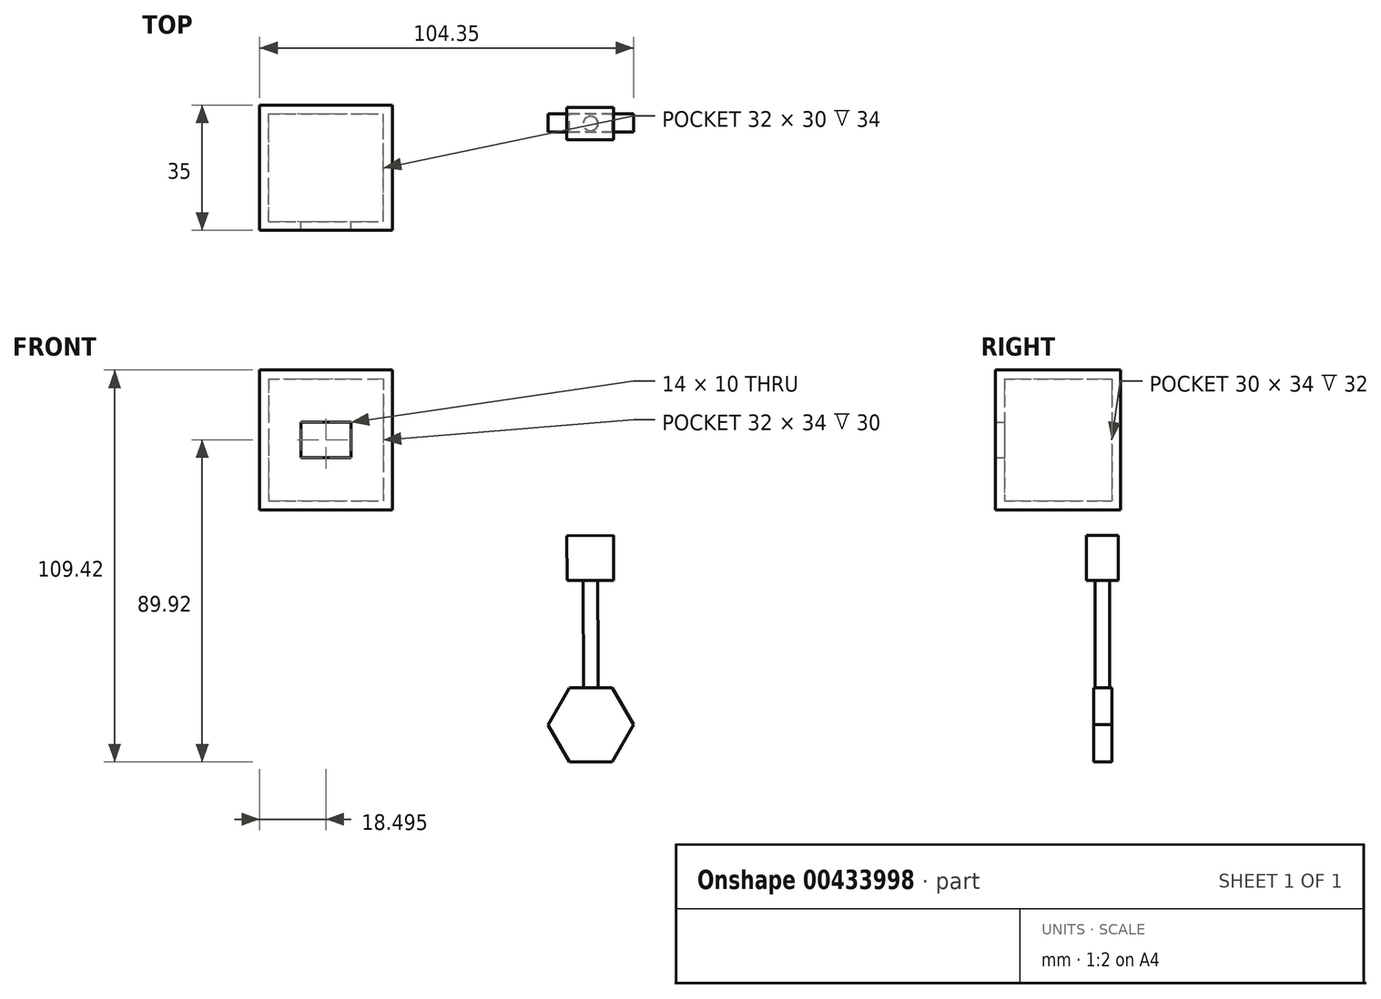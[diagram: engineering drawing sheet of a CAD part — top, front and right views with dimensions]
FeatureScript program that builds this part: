
annotation { "Feature Type Name" : "Feature", "Feature Type Description" : "" }
export const myFeature = defineFeature(function(context is Context, id is Id, definition is map)
    precondition{}
    {
        {
            var Q0;
            Q0=qCreatedBy(makeId("Front.planeOp"),FACE);
            var sketch = newSketch(context, id + "F0", { "sketchPlane" : qUnion([Q0])});
            skLineSegment(sketch, "E0.bottom", {"start": v(-54.76, 59.69) * mm, "end": v(-22.76, 59.69) * mm});
            skLineSegment(sketch, "E0.top", {"start": v(-54.76, 25.69) * mm, "end": v(-22.76, 25.69) * mm});
            skLineSegment(sketch, "E0.left", {"start": v(-54.76, 59.69) * mm, "end": v(-54.76, 25.69) * mm});
            skLineSegment(sketch, "E0.right", {"start": v(-22.76, 59.69) * mm, "end": v(-22.76, 25.69) * mm});
            skLineSegment(sketch, "E1.bottom", {"start": v(-45.76, 47.69) * mm, "end": v(-31.76, 47.69) * mm});
            skLineSegment(sketch, "E1.top", {"start": v(-45.76, 37.69) * mm, "end": v(-31.76, 37.69) * mm});
            skLineSegment(sketch, "E1.left", {"start": v(-45.76, 47.69) * mm, "end": v(-45.76, 37.69) * mm});
            skLineSegment(sketch, "E1.right", {"start": v(-31.76, 47.69) * mm, "end": v(-31.76, 37.69) * mm});
            skSolve(sketch);
        }
        {
            var Q0;
            Q0=makeQuery(id+"F0.imprint","IMPRINT",FACE,{"disambiguationData":[TD([[makeQuery(id+"F0.imprint","IMPRINT",EDGE,{"derivedFrom":sQuery(id+"F0.wireOp",EDGE,"E1.bottom")}),-1.0]])]});
            extrude(context, id + "F1", {"entities" : qUnion([Q0]), "depth" : 20 * mm});
        }
        {
            var Q0;
            Q0 = qSketchRegion(id + "F0", true);
            extrude(context, id + "F2", {"entities" : qUnion([Q0]), "operationType" : NewBodyOperationType.ADD, "depth" : 30 * mm});
        }
        {
            var Q0;
            Q0=makeQuery(id+"F2.opExtrude","SWEPT_FACE",FACE,{"disambiguationData":[OSD([sQuery(id+"F0.wireOp",EDGE,"E1.bottom")])]});
            var Q1;
            Q1=makeQuery(id+"F2.opExtrude","SWEPT_FACE",FACE,{"disambiguationData":[OSD([sQuery(id+"F0.wireOp",EDGE,"E1.right")])]});
            var Q2;
            Q2=makeQuery(id+"F2.opExtrude","SWEPT_FACE",FACE,{"disambiguationData":[OSD([sQuery(id+"F0.wireOp",EDGE,"E1.top")])]});
            var Q3;
            Q3=makeQuery(id+"F2.opExtrude","SWEPT_FACE",FACE,{"disambiguationData":[OSD([sQuery(id+"F0.wireOp",EDGE,"E1.left")])]});
            var Q4;
            Q4=makeQuery(id+"F1.opExtrude","CAP_FACE",FACE,{"disambiguationData":[OSD([sQuery(id+"F0.wireOp",EDGE,"E1.bottom"),sQuery(id+"F0.wireOp",EDGE,"E1.top"),sQuery(id+"F0.wireOp",EDGE,"E1.left"),sQuery(id+"F0.wireOp",EDGE,"E1.right")])],"isStart":false});
            shell(context, id + "F3", {"entities" : qUnion([Q0, Q1, Q2, Q3, Q4]), "thickness" : 2.5 * mm, "oppositeDirection" : true});
        }
        {
            var Q0;
            Q0=qCreatedBy(makeId("Front.planeOp"),FACE);
            var sketch = newSketch(context, id + "F4", { "sketchPlane" : qUnion([Q0])});
            skCircle(sketch, "E2.cCircle", {"center": v(35.15, -36.86) * mm, "radius": 10.34 * mm, "construction": true});
            skLineSegment(sketch, "E2.0", {"start": v(47.1, -36.81) * mm, "end": v(41.17, -47.17) * mm});
            skLineSegment(sketch, "E2.1", {"start": v(41.17, -47.17) * mm, "end": v(29.23, -47.23) * mm});
            skLineSegment(sketch, "E2.2", {"start": v(29.23, -47.23) * mm, "end": v(23.22, -36.92) * mm});
            skLineSegment(sketch, "E2.3", {"start": v(23.22, -36.92) * mm, "end": v(29.14, -26.55) * mm});
            skLineSegment(sketch, "E2.4", {"start": v(29.14, -26.55) * mm, "end": v(41.08, -26.5) * mm});
            skLineSegment(sketch, "E2.5", {"start": v(41.08, -26.5) * mm, "end": v(47.1, -36.81) * mm});
            skPoint(sketch, "E2.0.midPoint", {"position": v(44.13, -42) * mm});
            skSolve(sketch);
        }
        {
            var Q0;
            Q0=makeQuery(id+"F4.imprint","IMPRINT",FACE,{"disambiguationData":[TD([[makeQuery(id+"F4.imprint","IMPRINT",EDGE,{"derivedFrom":sQuery(id+"F4.wireOp",EDGE,"E2.0")}),-1.0]])]});
            extrude(context, id + "F5", {"entities" : qUnion([Q0]), "depth" : 5 * mm});
        }
        {
            var Q0;
            Q0=makeQuery(id+"F5.opExtrude","SWEPT_FACE",FACE,{"disambiguationData":[OSD([sQuery(id+"F4.wireOp",EDGE,"E2.4")])]});
            var sketch = newSketch(context, id + "F6", { "sketchPlane" : qUnion([Q0])});
            skCircle(sketch, "E3", {"center": v(35.06, -2.63) * mm, "radius": 2.03 * mm});
            skSolve(sketch);
        }
        {
            var Q0;
            Q0=makeQuery(id+"F6.imprint","IMPRINT",FACE,{"disambiguationData":[TD([[makeQuery(id+"F6.imprint","IMPRINT",EDGE,{"derivedFrom":sQuery(id+"F6.wireOp",EDGE,"E3")}),1.0]])]});
            extrude(context, id + "F7", {"entities" : qUnion([Q0]), "operationType" : NewBodyOperationType.ADD, "depth" : 30 * mm});
        }
        {
            var Q0;
            Q0=makeQuery(id+"F7.opExtrude","CAP_FACE",FACE,{"disambiguationData":[OSD([sQuery(id+"F6.wireOp",EDGE,"E3")])],"isStart":false});
            var sketch = newSketch(context, id + "F8", { "sketchPlane" : qUnion([Q0])});
            skLineSegment(sketch, "E4.bottom", {"start": v(28.56, 1.87) * mm, "end": v(41.56, 1.87) * mm});
            skLineSegment(sketch, "E4.top", {"start": v(28.56, -7.13) * mm, "end": v(41.56, -7.13) * mm});
            skLineSegment(sketch, "E4.left", {"start": v(28.56, 1.87) * mm, "end": v(28.56, -7.13) * mm});
            skLineSegment(sketch, "E4.right", {"start": v(41.56, 1.87) * mm, "end": v(41.56, -7.13) * mm});
            skPoint(sketch, "E4.middle", {"position": v(35.06, -2.63) * mm});
            skSolve(sketch);
        }
        {
            var Q0;
            Q0 = qSketchRegion(id + "F8", true);
            extrude(context, id + "F9", {"entities" : qUnion([Q0]), "operationType" : NewBodyOperationType.ADD, "depth" : 12.5 * mm});
        }
    });
